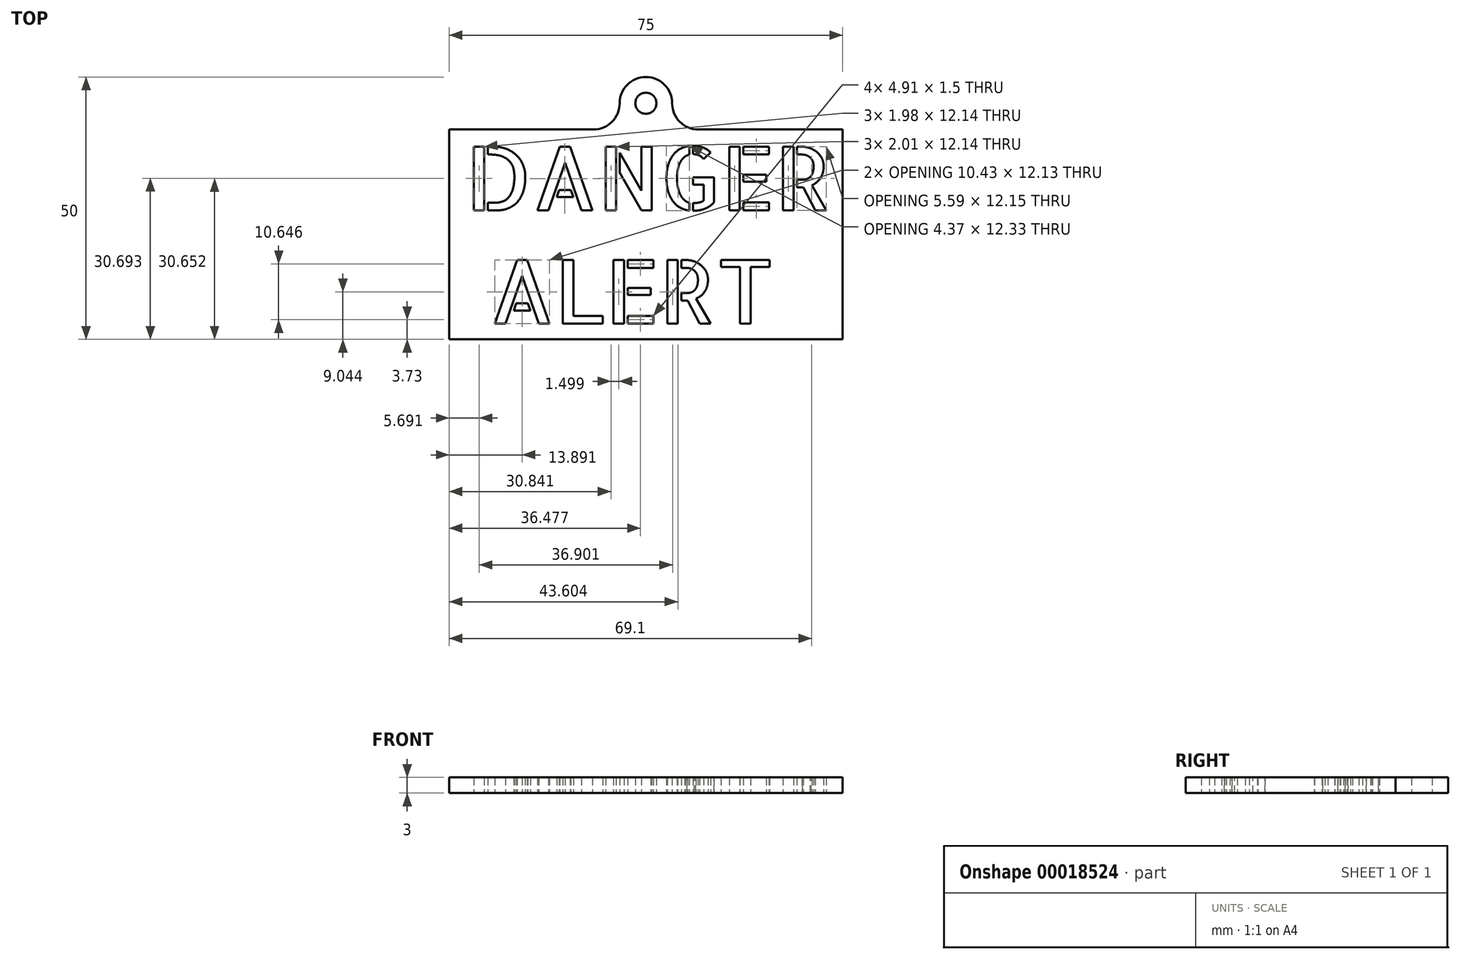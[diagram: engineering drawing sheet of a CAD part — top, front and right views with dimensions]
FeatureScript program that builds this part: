
annotation { "Feature Type Name" : "Feature", "Feature Type Description" : "" }
export const myFeature = defineFeature(function(context is Context, id is Id, definition is map)
    precondition{}
    {
        {
            var Q0;
            Q0=qCreatedBy(makeId("Top.planeOp"),FACE);
            var sketch = newSketch(context, id + "F0", { "sketchPlane" : qUnion([Q0])});
            skLineSegment(sketch, "E0.bottom", {"start": v(-37.5, 20) * mm, "end": v(-10, 20) * mm});
            skLineSegment(sketch, "E0.top", {"start": v(-37.5, -20) * mm, "end": v(37.5, -20) * mm});
            skLineSegment(sketch, "E0.left", {"start": v(-37.5, 20) * mm, "end": v(-37.5, -20) * mm});
            skLineSegment(sketch, "E0.right", {"start": v(37.5, 20) * mm, "end": v(37.5, -20) * mm});
            skText(sketch, "E1", { "text": "DANGER\n ALERT", "fontName": "AllertaStencil-Regular.ttf"});
            skCircle(sketch, "E2", {"center": v(0, 25) * mm, "radius": 2 * mm});
            skArc(sketch, "E3", {"start": v(5, 25) * mm, "mid": v(0, 30) * mm, "end": v(-5, 25) * mm});
            skArc(sketch, "E4", {"start": v(-10, 20) * mm, "mid": v(-6.46, 21.46) * mm, "end": v(-5, 25) * mm});
            skArc(sketch, "E5.MirrorCS", {"start": v(10, 20) * mm, "mid": v(6.46, 21.46) * mm, "end": v(5, 25) * mm});
            skLineSegment(sketch, "E6.trimOffspring", {"start": v(10, 20) * mm, "end": v(37.5, 20) * mm});
            const initialGuessF0  = {"E1": [-0.03438, 0.00458, 1, 0, 0.01215]};
            skSetInitialGuess(sketch, initialGuessF0);
            skSolve(sketch);
        }
        {
            var Q0;
            Q0=makeQuery(id+"F0.imprint","IMPRINT",FACE,{"disambiguationData":[TD([[makeQuery(id+"F0.imprint","IMPRINT",EDGE,{"derivedFrom":sQuery(id+"F0.wireOp",EDGE,"E0.bottom")}),-1.0]])]});
            extrude(context, id + "F1", {"entities" : qUnion([Q0]), "depth" : 3 * mm});
        }
    });
